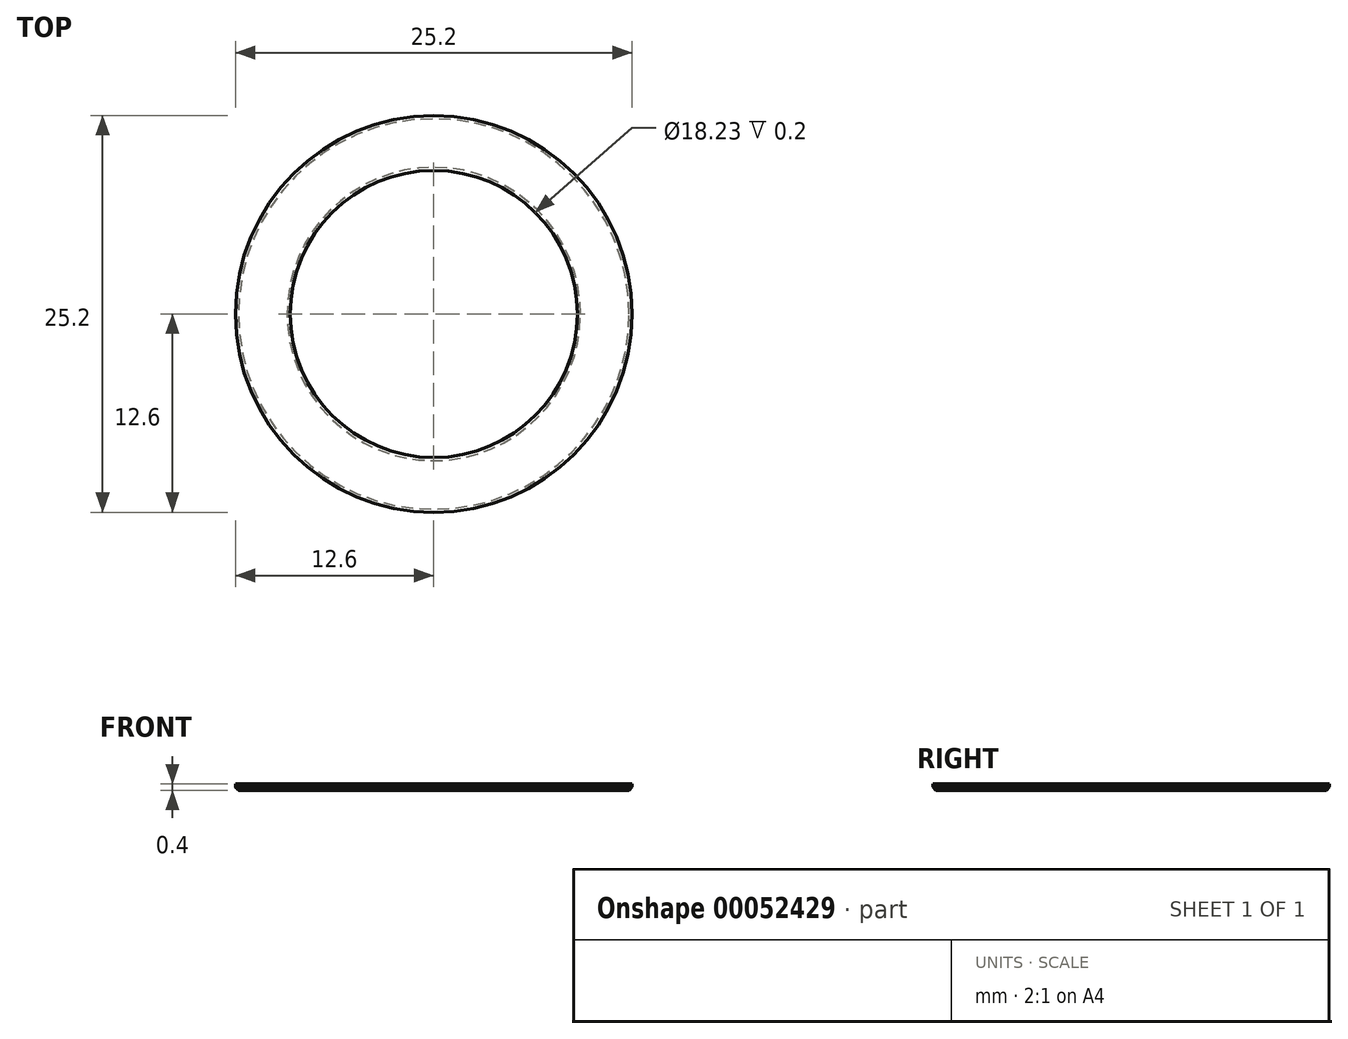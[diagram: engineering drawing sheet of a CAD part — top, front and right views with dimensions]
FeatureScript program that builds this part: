
annotation { "Feature Type Name" : "Feature", "Feature Type Description" : "" }
export const myFeature = defineFeature(function(context is Context, id is Id, definition is map)
    precondition{}
    {
        {
            var Q0;
            Q0=qCreatedBy(makeId("Front.planeOp"),FACE);
            var sketch = newSketch(context, id + "F0", { "sketchPlane" : qUnion([Q0])});
            skLineSegment(sketch, "E0.bottom", {"start": v(-9.12, 0) * mm, "end": v(-12.6, 0) * mm});
            skLineSegment(sketch, "E0.top", {"start": v(-9.12, 0.4) * mm, "end": v(-12.6, 0.4) * mm});
            skLineSegment(sketch, "E0.left", {"start": v(-9.12, 0) * mm, "end": v(-9.12, 0.4) * mm});
            skLineSegment(sketch, "E0.right", {"start": v(-12.6, 0) * mm, "end": v(-12.6, 0.4) * mm});
            skLineSegment(sketch, "E1", {"start": v(0, 0) * mm, "end": v(0, 2.9) * mm});
            skSolve(sketch);
        }
        {
            var Q0;
            Q0=makeQuery(id+"F0.imprint","IMPRINT",FACE,{"disambiguationData":[TD([[makeQuery(id+"F0.imprint","IMPRINT",EDGE,{"derivedFrom":sQuery(id+"F0.wireOp",EDGE,"E0.bottom")}),-1.0]])]});
            var Q1;
            Q1=sQuery(id+"F0.wireOp",EDGE,"E1");
            revolve(context, id + "F1", {"surfaceOperationType" : NewSurfaceOperationType.NEW, "entities" : qUnion([Q0]), "axis" : qUnion([Q1]), "revolveType" : RevolveType.FULL});
        }
        {
            var Q0;
            Q0=makeQuery(id+"F1.opRevolve","SWEPT_FACE",FACE,{"disambiguationData":[OSD([sQuery(id+"F0.wireOp",EDGE,"E0.bottom")])]});
            chamfer(context, id + "F2", {"entities" : qUnion([Q0]), "width" : 0.2 * mm});
        }
    });
